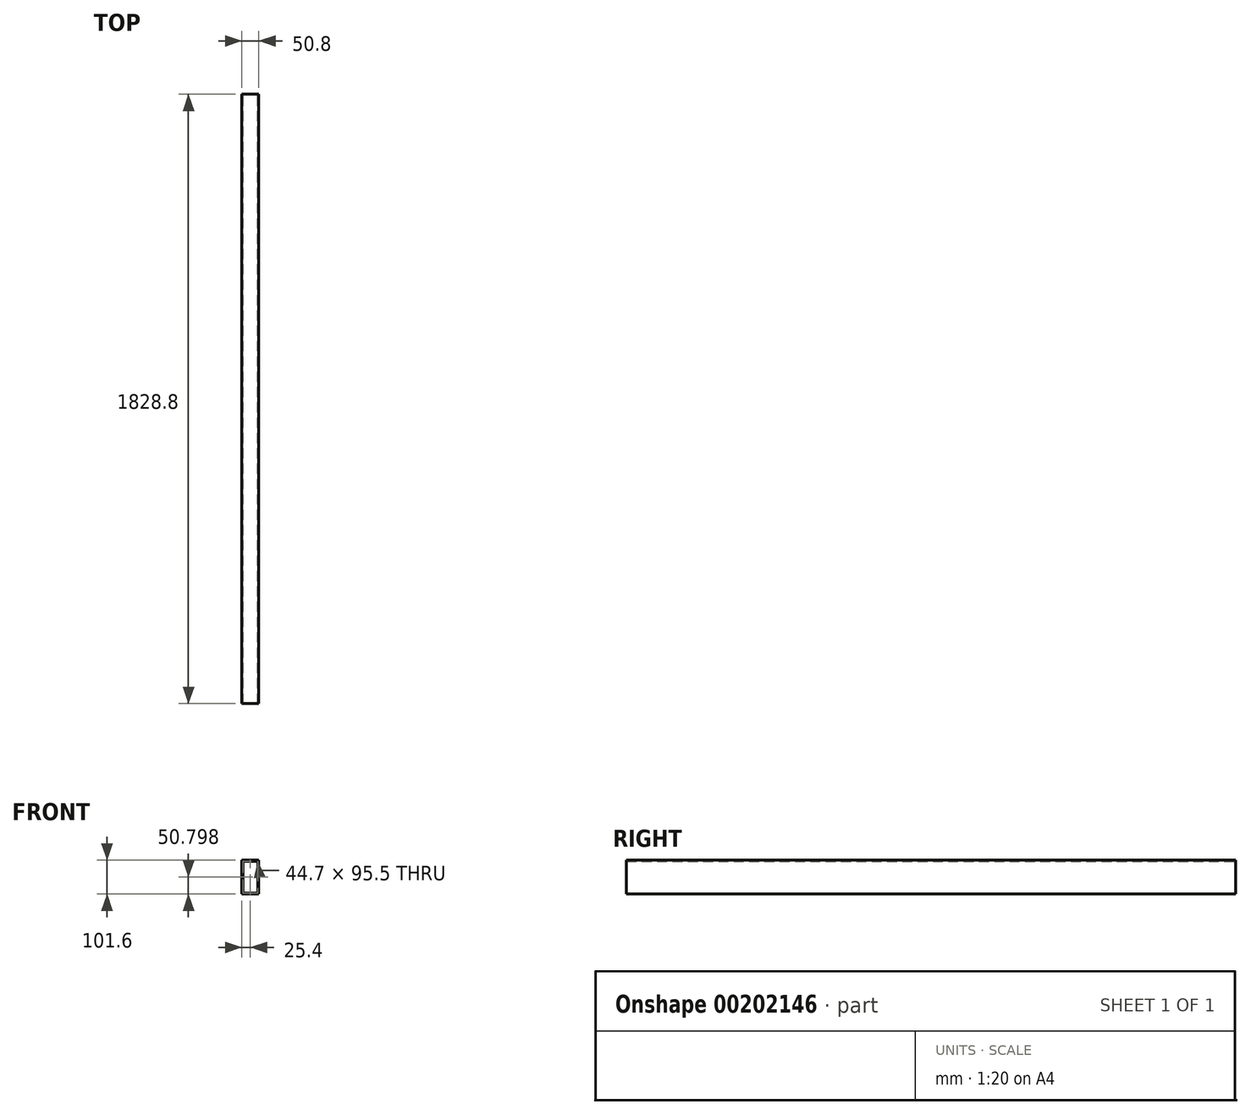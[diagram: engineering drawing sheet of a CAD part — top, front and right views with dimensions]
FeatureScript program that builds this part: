
annotation { "Feature Type Name" : "Feature", "Feature Type Description" : "" }
export const myFeature = defineFeature(function(context is Context, id is Id, definition is map)
    precondition{}
    {
        {
            var Q0;
            Q0=qCreatedBy(makeId("Front.planeOp"),FACE);
            var sketch = newSketch(context, id + "F0", { "sketchPlane" : qUnion([Q0])});
            skLineSegment(sketch, "E0.bottom", {"start": v(-25.3, 56.39) * mm, "end": v(25.5, 56.39) * mm});
            skLineSegment(sketch, "E0.top", {"start": v(-25.3, -45.21) * mm, "end": v(25.5, -45.21) * mm});
            skLineSegment(sketch, "E0.left", {"start": v(-25.3, 56.39) * mm, "end": v(-25.3, -45.21) * mm});
            skLineSegment(sketch, "E0.right", {"start": v(25.5, 56.39) * mm, "end": v(25.5, -45.21) * mm});
            skLineSegment(sketch, "E1.bottom", {"start": v(-22.25, 53.34) * mm, "end": v(22.45, 53.34) * mm});
            skLineSegment(sketch, "E1.top", {"start": v(-22.25, -42.16) * mm, "end": v(22.45, -42.16) * mm});
            skLineSegment(sketch, "E1.left", {"start": v(-22.25, 53.34) * mm, "end": v(-22.25, -42.16) * mm});
            skLineSegment(sketch, "E1.right", {"start": v(22.45, 53.34) * mm, "end": v(22.45, -42.16) * mm});
            skSolve(sketch);
        }
        {
            var Q0;
            Q0=makeQuery(id+"F0.imprint","IMPRINT",FACE,{"disambiguationData":[TD([[makeQuery(id+"F0.imprint","IMPRINT",EDGE,{"derivedFrom":sQuery(id+"F0.wireOp",EDGE,"E0.bottom")}),-1.0]])]});
            extrude(context, id + "F1", {"entities" : qUnion([Q0]), "depth" : 1828.8 * mm});
        }
    });
